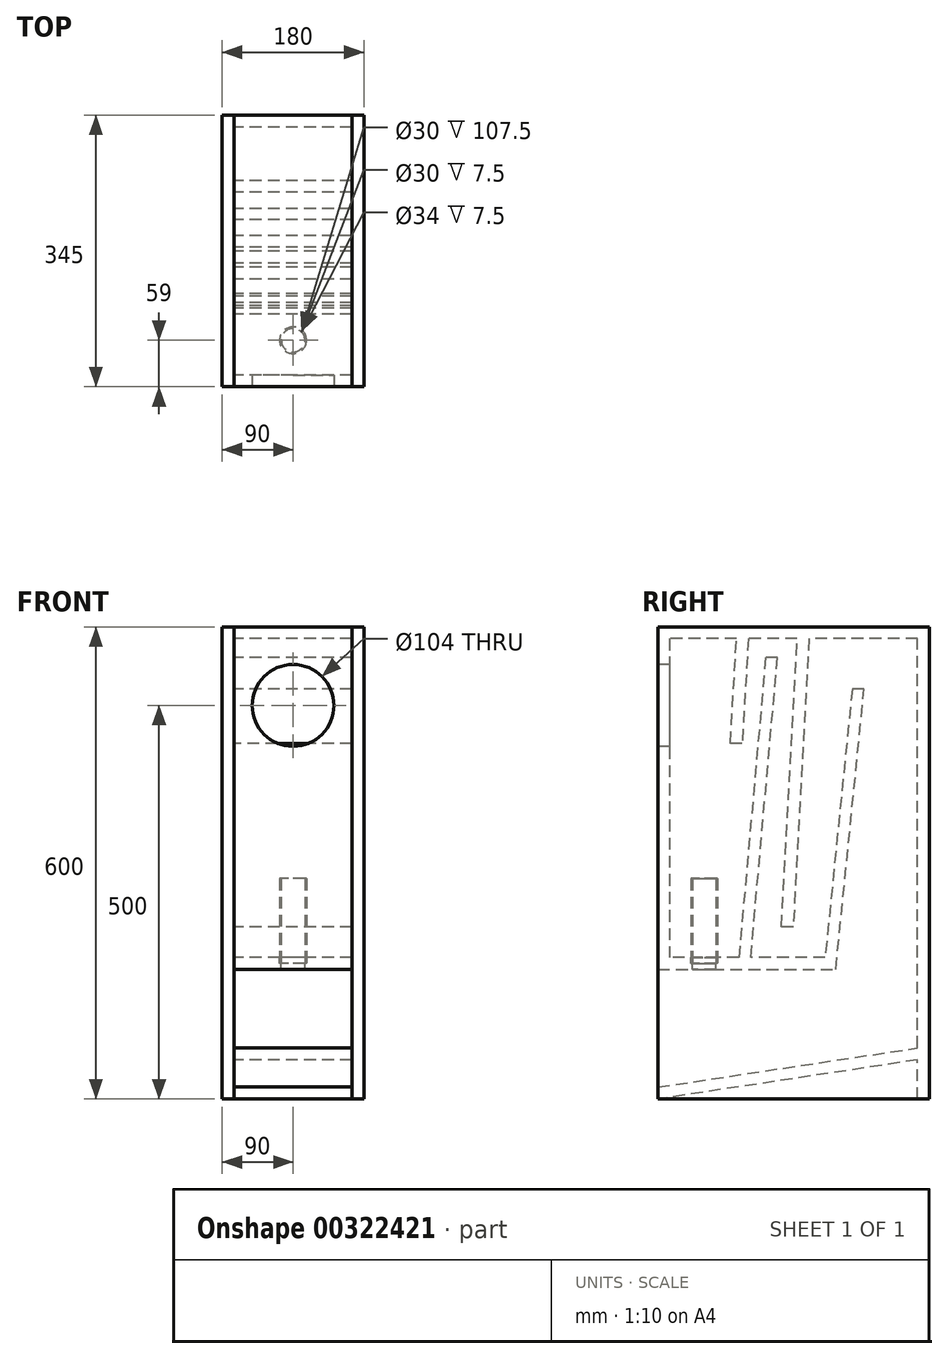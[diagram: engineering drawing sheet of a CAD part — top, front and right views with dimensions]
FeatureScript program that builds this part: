
annotation { "Feature Type Name" : "Feature", "Feature Type Description" : "" }
export const myFeature = defineFeature(function(context is Context, id is Id, definition is map)
    precondition{}
    {
        {
            var Q0;
            Q0=qCreatedBy(makeId("Right.planeOp"),FACE);
            var sketch = newSketch(context, id + "F0", { "sketchPlane" : qUnion([Q0])});
            skLineSegment(sketch, "E0", {"start": v(0, -335) * mm, "end": v(0, 100) * mm});
            skLineSegment(sketch, "E1", {"start": v(0, 100) * mm, "end": v(345, 100) * mm});
            skLineSegment(sketch, "E2", {"start": v(345, 100) * mm, "end": v(345, -500) * mm});
            skLineSegment(sketch, "E3", {"start": v(345, -500) * mm, "end": v(330, -500) * mm});
            skLineSegment(sketch, "E4", {"start": v(330, -500) * mm, "end": v(330, -450.17) * mm});
            skLineSegment(sketch, "E5", {"start": v(330, -450.17) * mm, "end": v(0, -500) * mm});
            skLineSegment(sketch, "E6", {"start": v(0, -500) * mm, "end": v(0, -484.83) * mm});
            skLineSegment(sketch, "E7", {"start": v(0, -484.83) * mm, "end": v(330, -435) * mm});
            skLineSegment(sketch, "E8", {"start": v(330, -435) * mm, "end": v(330, 85) * mm});
            skLineSegment(sketch, "E9", {"start": v(330, 85) * mm, "end": v(192, 85) * mm});
            skLineSegment(sketch, "E10", {"start": v(192, 85) * mm, "end": v(172, -281) * mm});
            skLineSegment(sketch, "E11", {"start": v(172, -281) * mm, "end": v(156.98, -281) * mm});
            skLineSegment(sketch, "E12", {"start": v(156.98, -281) * mm, "end": v(176.98, 85) * mm});
            skLineSegment(sketch, "E13", {"start": v(176.98, 85) * mm, "end": v(115, 85) * mm});
            skLineSegment(sketch, "E14", {"start": v(115, 85) * mm, "end": v(107, -48) * mm});
            skLineSegment(sketch, "E15", {"start": v(107, -48) * mm, "end": v(91.97, -48) * mm});
            skLineSegment(sketch, "E16", {"start": v(91.97, -48) * mm, "end": v(99.97, 85) * mm});
            skLineSegment(sketch, "E17", {"start": v(99.97, 85) * mm, "end": v(15, 85) * mm});
            skLineSegment(sketch, "E18", {"start": v(15, 85) * mm, "end": v(15, -320) * mm});
            skLineSegment(sketch, "E19", {"start": v(0, -335) * mm, "end": v(226, -335) * mm});
            skLineSegment(sketch, "E20", {"start": v(226, -335) * mm, "end": v(262, 21) * mm});
            skLineSegment(sketch, "E21", {"start": v(262, 21) * mm, "end": v(246.92, 21) * mm});
            skLineSegment(sketch, "E22", {"start": v(246.92, 21) * mm, "end": v(212.44, -320) * mm});
            skLineSegment(sketch, "E23", {"start": v(212.44, -320) * mm, "end": v(118, -320) * mm});
            skLineSegment(sketch, "E24", {"start": v(118, -320) * mm, "end": v(152, 61) * mm});
            skLineSegment(sketch, "E25", {"start": v(152, 61) * mm, "end": v(136.94, 61) * mm});
            skLineSegment(sketch, "E26", {"start": v(136.94, 61) * mm, "end": v(102.94, -320) * mm});
            skLineSegment(sketch, "E27", {"start": v(102.94, -320) * mm, "end": v(15, -320) * mm});
            skSolve(sketch);
        }
        {
            var Q0;
            Q0=makeQuery(id+"F0.imprint","IMPRINT",FACE,{"disambiguationData":[TD([[makeQuery(id+"F0.imprint","IMPRINT",EDGE,{"derivedFrom":sQuery(id+"F0.wireOp",EDGE,"E0")}),-1.0]])]});
            extrude(context, id + "F1", {"entities" : qUnion([Q0]), "endBound" : BoundingType.SYMMETRIC, "depth" : 150 * mm});
        }
        {
            var Q0;
            Q0=makeQuery(id+"F1.opExtrude","SWEPT_FACE",FACE,{"disambiguationData":[OSD([sQuery(id+"F0.wireOp",EDGE,"E0")])]});
            var sketch = newSketch(context, id + "F2", { "sketchPlane" : qUnion([Q0])});
            skCircle(sketch, "E28", {"center": v(0, 0) * mm, "radius": 52 * mm});
            skSolve(sketch);
        }
        {
            var Q0;
            Q0=makeQuery(id+"F2.imprint","IMPRINT",FACE,{"disambiguationData":[TD([[makeQuery(id+"F2.imprint","IMPRINT",EDGE,{"derivedFrom":sQuery(id+"F2.wireOp",EDGE,"E28")}),1.0]])]});
            extrude(context, id + "F3", {"entities" : qUnion([Q0]), "operationType" : NewBodyOperationType.REMOVE, "endBound" : BoundingType.UP_TO_NEXT, "oppositeDirection" : true, "depth" : 25 * mm});
        }
        {
            var Q0;
            Q0=makeQuery(id+"F1.opExtrude","CAP_FACE",FACE,{"disambiguationData":[OSD([sQuery(id+"F0.wireOp",EDGE,"E0"),sQuery(id+"F0.wireOp",EDGE,"E1"),sQuery(id+"F0.wireOp",EDGE,"E2"),sQuery(id+"F0.wireOp",EDGE,"E3"),sQuery(id+"F0.wireOp",EDGE,"E4"),sQuery(id+"F0.wireOp",EDGE,"E5"),sQuery(id+"F0.wireOp",EDGE,"E6"),sQuery(id+"F0.wireOp",EDGE,"E7"),sQuery(id+"F0.wireOp",EDGE,"E8"),sQuery(id+"F0.wireOp",EDGE,"E9"),sQuery(id+"F0.wireOp",EDGE,"E10"),sQuery(id+"F0.wireOp",EDGE,"E11"),sQuery(id+"F0.wireOp",EDGE,"E12"),sQuery(id+"F0.wireOp",EDGE,"E13"),sQuery(id+"F0.wireOp",EDGE,"E14"),sQuery(id+"F0.wireOp",EDGE,"E15"),sQuery(id+"F0.wireOp",EDGE,"E16"),sQuery(id+"F0.wireOp",EDGE,"E17"),sQuery(id+"F0.wireOp",EDGE,"E18"),sQuery(id+"F0.wireOp",EDGE,"E19"),sQuery(id+"F0.wireOp",EDGE,"E20"),sQuery(id+"F0.wireOp",EDGE,"E21"),sQuery(id+"F0.wireOp",EDGE,"E22"),sQuery(id+"F0.wireOp",EDGE,"E23"),sQuery(id+"F0.wireOp",EDGE,"E24"),sQuery(id+"F0.wireOp",EDGE,"E25"),sQuery(id+"F0.wireOp",EDGE,"E26"),sQuery(id+"F0.wireOp",EDGE,"E27")])],"isStart":false});
            var sketch = newSketch(context, id + "F4", { "sketchPlane" : qUnion([Q0])});
            skLineSegment(sketch, "E29.0", {"start": v(0, 100) * mm, "end": v(345, 100) * mm});
            skLineSegment(sketch, "E29.1", {"start": v(345, 100) * mm, "end": v(345, -500) * mm});
            skLineSegment(sketch, "E30.0", {"start": v(0, -500) * mm, "end": v(0, 100) * mm});
            skLineSegment(sketch, "E31.0", {"start": v(345, -500) * mm, "end": v(0, -500) * mm});
            skSolve(sketch);
        }
        {
            var Q0;
            Q0 = qSketchRegion(id + "F4", true);
            extrude(context, id + "F5", {"entities" : qUnion([Q0]), "depth" : 15 * mm});
        }
        {
            var Q0;
            Q0=makeQuery(id+"F5.opExtrude","SWEPT_BODY",BODY,{"disambiguationData":[OSD([sQuery(id+"F4.wireOp",EDGE,"E29.0"),sQuery(id+"F4.wireOp",EDGE,"E29.1"),sQuery(id+"F4.wireOp",EDGE,"E30.0"),sQuery(id+"F4.wireOp",EDGE,"E31.0")])]});
            var Q1;
            Q1=qCreatedBy(makeId("Right.planeOp"),FACE);
            mirror(context, id + "F6", {"entities" : qUnion([Q0]), "mirrorPlane" : qUnion([Q1])});
        }
        {
            var Q0;
            Q0=makeQuery(id+"F1.opExtrude","SWEPT_FACE",FACE,{"disambiguationData":[OSD([sQuery(id+"F0.wireOp",EDGE,"E27")])]});
            var sketch = newSketch(context, id + "F7", { "sketchPlane" : qUnion([Q0])});
            skCircle(sketch, "E32", {"center": v(0, 59) * mm, "radius": 17 * mm});
            skCircle(sketch, "E33", {"center": v(0, 59) * mm, "radius": 15 * mm});
            skSolve(sketch);
        }
        {
            var Q0;
            Q0=makeQuery(id+"F7.imprint","IMPRINT",FACE,{"disambiguationData":[TD([[makeQuery(id+"F7.imprint","IMPRINT",EDGE,{"derivedFrom":sQuery(id+"F7.wireOp",EDGE,"E33")}),1.0]])]});
            extrude(context, id + "F8", {"entities" : qUnion([Q0]), "operationType" : NewBodyOperationType.REMOVE, "endBound" : BoundingType.UP_TO_NEXT, "oppositeDirection" : true, "depth" : 25 * mm});
        }
        {
            var Q0;
            Q0=makeQuery(id+"F7.imprint","IMPRINT",FACE,{"disambiguationData":[TD([[makeQuery(id+"F7.imprint","IMPRINT",EDGE,{"derivedFrom":sQuery(id+"F7.wireOp",EDGE,"E32")}),1.0]])]});
            var Q1;
            Q1=sQuery(id+"F7.wireOp",EDGE,"E32");
            extrude(context, id + "F9", {"entities" : qUnion([Q0]), "operationType" : NewBodyOperationType.REMOVE, "surfaceEntities" : qUnion([Q1]), "oppositeDirection" : true, "depth" : 7.5 * mm});
        }
        {
            var Q0;
            Q0=makeQuery(id+"F9.boolean.opBoolean","COPY",FACE,{"derivedFrom":makeQuery(id+"F9.opExtrude","CAP_FACE",FACE,{"disambiguationData":[OSD([sQuery(id+"F7.wireOp",EDGE,"E32"),sQuery(id+"F7.wireOp",EDGE,"E33")])],"isStart":false})});
            extrude(context, id + "F10", {"entities" : qUnion([Q0]), "depth" : (115 - 7.5) * mm});
        }
    });
